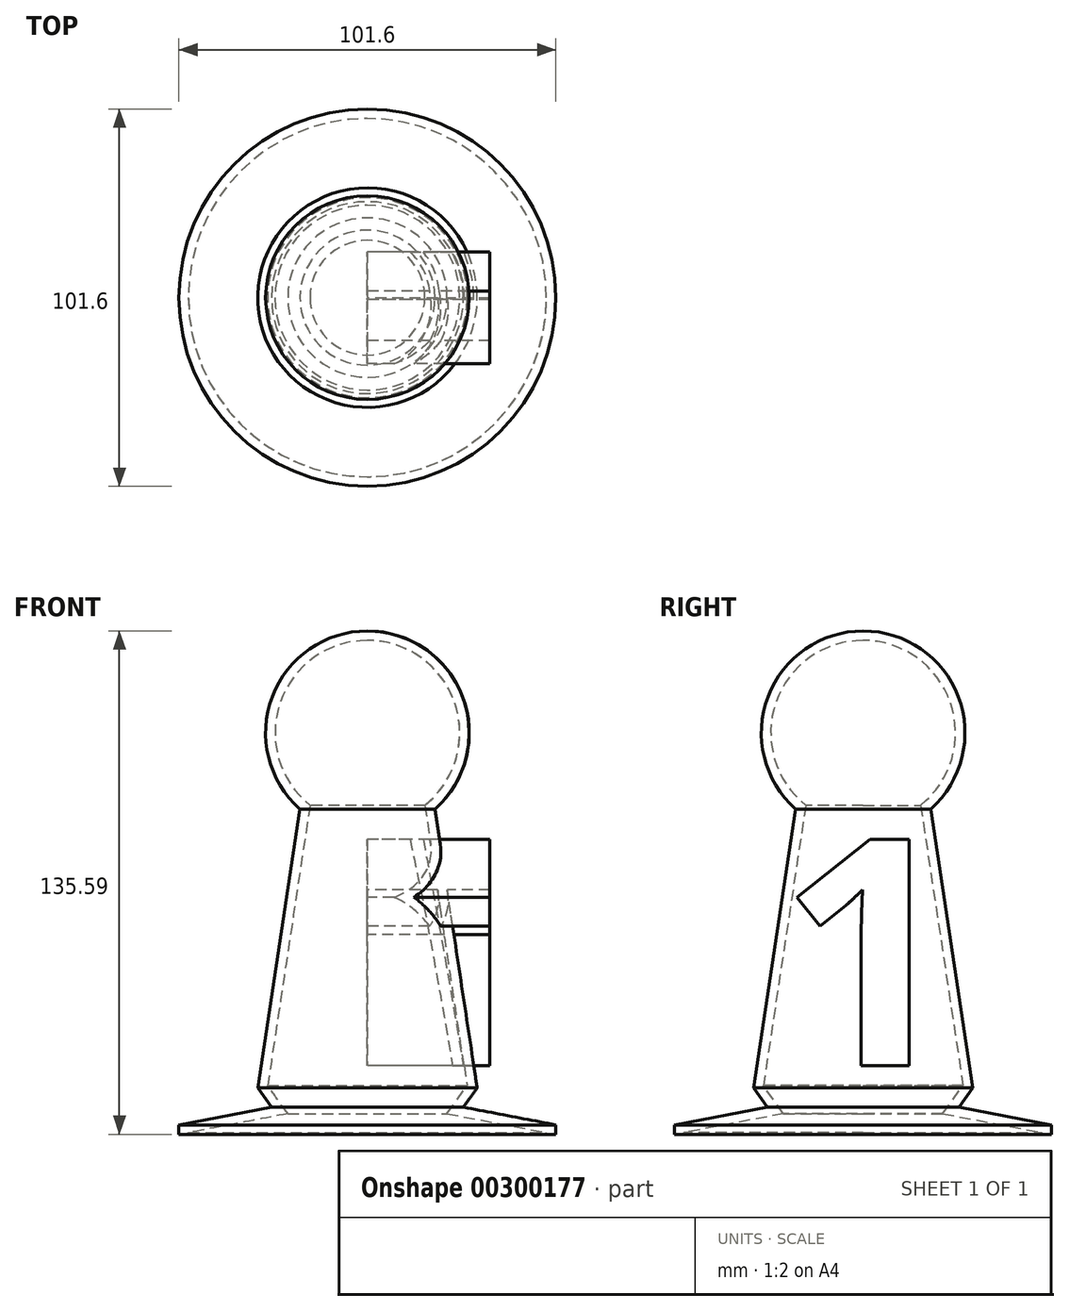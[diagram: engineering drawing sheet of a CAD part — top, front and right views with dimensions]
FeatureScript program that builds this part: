
annotation { "Feature Type Name" : "Feature", "Feature Type Description" : "" }
export const myFeature = defineFeature(function(context is Context, id is Id, definition is map)
    precondition{}
    {
        {
            var Q0;
            Q0=qCreatedBy(makeId("Front.planeOp"),FACE);
            var sketch = newSketch(context, id + "F0", { "sketchPlane" : qUnion([Q0])});
            skLineSegment(sketch, "E0", {"start": v(0, -75.09) * mm, "end": v(-50.8, -75.09) * mm});
            skLineSegment(sketch, "E1", {"start": v(-50.8, -75.09) * mm, "end": v(-50.8, -72.55) * mm});
            skLineSegment(sketch, "E2", {"start": v(-50.8, -72.55) * mm, "end": v(-25.85, -67.78) * mm});
            skLineSegment(sketch, "E3", {"start": v(-29.57, -62.62) * mm, "end": v(-18.2, 12.54) * mm});
            skArc(sketch, "E4", {"start": v(0, 60.5) * mm, "mid": v(-25.65, 42.8) * mm, "end": v(-18.2, 12.54) * mm});
            skLineSegment(sketch, "E5", {"start": v(-29.57, -62.62) * mm, "end": v(-25.85, -67.78) * mm});
            skLineSegment(sketch, "E6", {"start": v(0, 60.5) * mm, "end": v(0, -75.09) * mm});
            skSolve(sketch);
        }
        {
            var Q0;
            Q0 = qSketchRegion(id + "F0", true);
            var Q1;
            Q1=sQuery(id+"F0.wireOp",EDGE,"E6");
            revolve(context, id + "F1", {"entities" : qUnion([Q0]), "axis" : qUnion([Q1]), "revolveType" : RevolveType.FULL});
        }
        {
            var Q0;
            Q0=makeQuery(id+"F1.opRevolve","SWEPT_FACE",FACE,{"disambiguationData":[OSD([sQuery(id+"F0.wireOp",EDGE,"E0")])]});
            shell(context, id + "F2", {"entities" : qUnion([Q0]), "thickness" : 2.54 * mm});
        }
        {
            var Q0;
            Q0=qCreatedBy(makeId("Right.planeOp"),FACE);
            var sketch = newSketch(context, id + "F3", { "sketchPlane" : qUnion([Q0])});
            skText(sketch, "E7", { "text": "1", "fontName": "OpenSans-Bold.ttf"});
            const initialGuessF3  = {"E7": [-0.02287, -0.05654, 1, 0, 0.06141]};
            skSetInitialGuess(sketch, initialGuessF3);
            skSolve(sketch);
        }
        {
            var Q0;
            Q0 = qSketchRegion(id + "F3", true);
            extrude(context, id + "F4", {"entities" : qUnion([Q0]), "operationType" : NewBodyOperationType.ADD, "depth" : 33.02 * mm});
        }
    });
